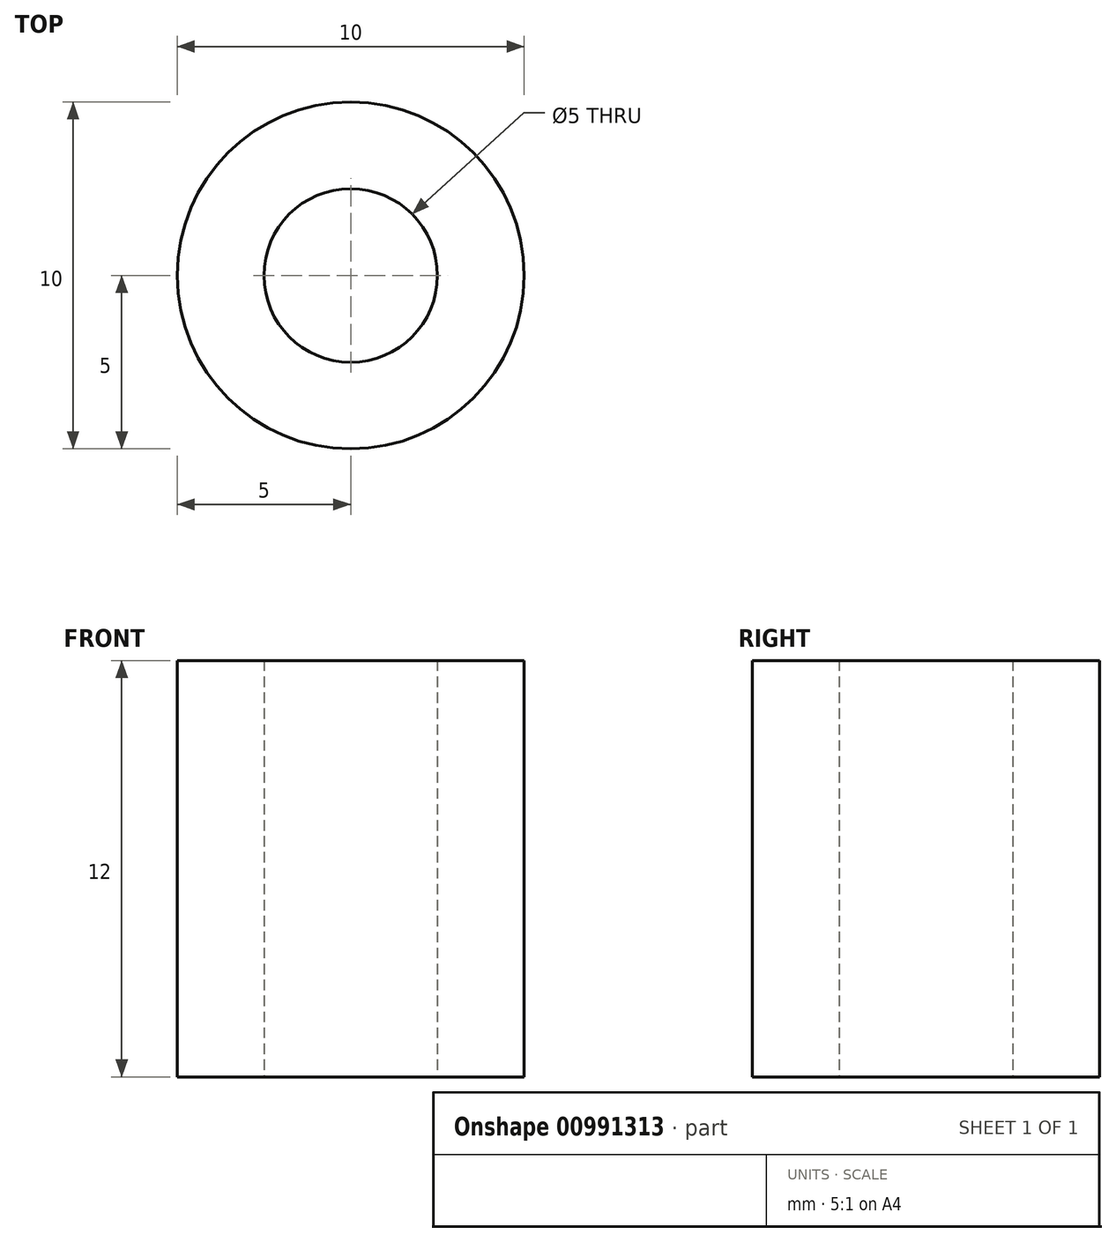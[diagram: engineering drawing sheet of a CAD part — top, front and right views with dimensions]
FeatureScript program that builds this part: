
annotation { "Feature Type Name" : "Feature", "Feature Type Description" : "" }
export const myFeature = defineFeature(function(context is Context, id is Id, definition is map)
    precondition{}
    {
        {
            var Q0;
            Q0=qCreatedBy(makeId("Top.planeOp"),FACE);
            var sketch = newSketch(context, id + "F0", { "sketchPlane" : qUnion([Q0])});
            skCircle(sketch, "E0", {"center": v(0, 0) * mm, "radius": 5 * mm});
            skCircle(sketch, "E1", {"center": v(0, 0) * mm, "radius": 2.5 * mm});
            skSolve(sketch);
        }
        {
            var Q0;
            Q0 = qSketchRegion(id + "F0", true);
            extrude(context, id + "F1", {"entities" : qUnion([Q0]), "depth" : 12 * mm, "offsetDistance" : 25 * mm});
        }
    });
